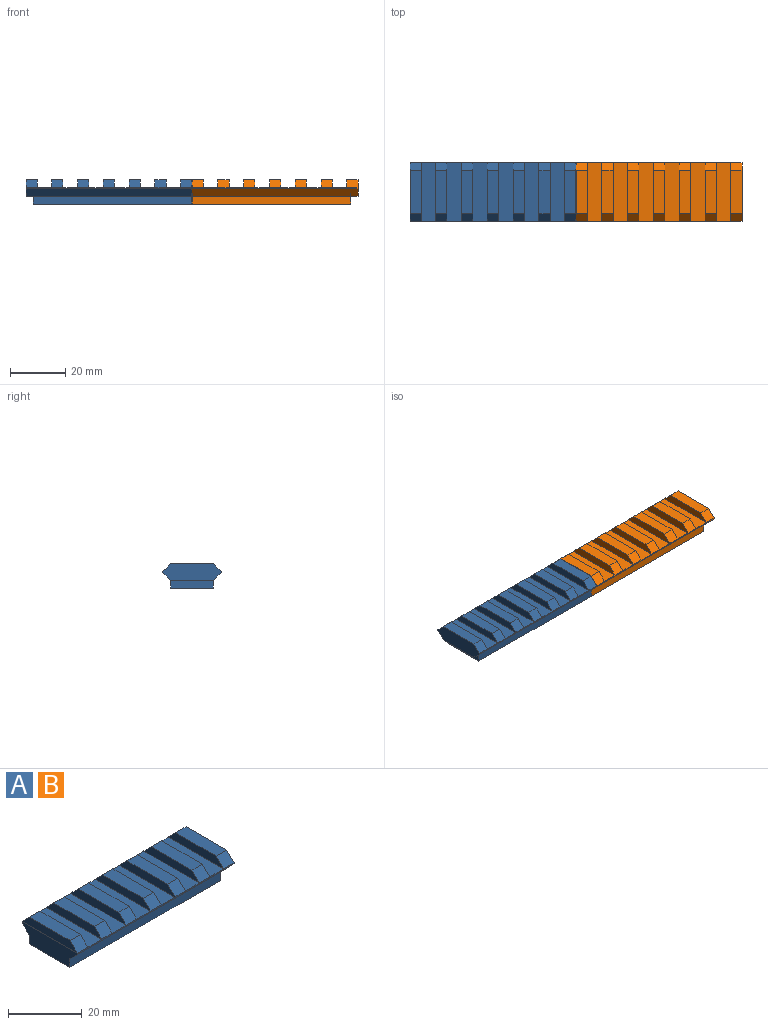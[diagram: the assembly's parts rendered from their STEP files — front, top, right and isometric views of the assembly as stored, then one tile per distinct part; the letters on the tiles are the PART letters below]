
ASSEMBLY  parts=2 mates=1
PART A: 54 faces, bbox 60.2x21.2x8.9 mm
  f0: plane 21.2x5.99mm, normal (-1,0,0), area 103mm2, adj f1,f3,f5,f6,f34,f44,f51,f52
  f1: plane 57.6x15.57mm, normal (0,0,-1), area 897.1mm2, adj f0,f2,f51,f53
  f2: plane 18.39x5.66mm, normal (1,0,0), area 44.7mm2, adj f1,f3,f5,f35,f37,f44,f51,f52
  f3: plane 57.6x2.79mm, normal (0,-0.71,-0.71), area 227.7mm2, adj f0,f2,f5,f52
  f4: plane 15.6x4.01mm, normal (0,0,1), area 62.4mm2, adj f11,f12,f13,f50
  f5: plane 60.17x0.4mm, normal (0,-1,0), area 22.1mm2, adj f0,f2,f3,f11,f12,f14,f15,f16
  f6: plane 60.17x0.4mm, normal (0,1,0), area 21.1mm2, adj f0,f11,f12,f13,f14,f15,f16,f17
  f7: plane 15.6x4.01mm, normal (0,0,1), area 62.4mm2, adj f15,f16,f17,f49
  f8: plane 15.6x4.01mm, normal (0,0,1), area 62.4mm2, adj f19,f20,f21,f48
  f9: plane 15.6x4.01mm, normal (0,0,1), area 62.4mm2, adj f36,f38,f39,f45
  f10: plane 15.6x4.01mm, normal (0,0,1), area 62.4mm2, adj f40,f41,f42,f43
  f11: plane 21.2x2.88mm, normal (-1,0,0), area 53.2mm2, adj f4,f5,f6,f13,f14,f50
  f12: plane 21.2x2.89mm, normal (1,0,0), area 53.1mm2, adj f4,f5,f6,f13,f18,f50
  f13: plane 4x2.8mm, normal (0,0.71,0.71), area 15.8mm2, adj f4,f6,f11,f12
  f14: plane 21.2x5.35mm, normal (0,0,1), area 113.4mm2, adj f5,f6,f11,f24
  f15: plane 21.2x2.88mm, normal (-1,0,0), area 53.2mm2, adj f5,f6,f7,f17,f18,f49
  f16: plane 21.2x2.89mm, normal (1,0,0), area 53.1mm2, adj f5,f6,f7,f17,f22,f49
  f17: plane 4x2.8mm, normal (0,0.71,0.71), area 15.8mm2, adj f6,f7,f15,f16
  f18: plane 21.2x5.35mm, normal (0,0,1), area 113.4mm2, adj f5,f6,f12,f15
  f19: plane 21.2x2.88mm, normal (-1,0,0), area 53.2mm2, adj f5,f6,f8,f21,f22,f48
  f20: plane 21.2x2.89mm, normal (1,0,0), area 53.1mm2, adj f5,f6,f8,f21,f23,f48
  f21: plane 4x2.8mm, normal (0,0.71,0.71), area 15.8mm2, adj f6,f8,f19,f20
  f22: plane 21.2x5.35mm, normal (0,0,1), area 113.4mm2, adj f5,f6,f16,f19
  f23: plane 21.2x5.35mm, normal (0,0,1), area 113.4mm2, adj f5,f6,f20,f40
  f24: plane 21.2x2.88mm, normal (1,0,0), area 53.2mm2, adj f5,f6,f14,f26,f27,f47
  f25: plane 21.2x2.88mm, normal (-1,0,0), area 53.1mm2, adj f5,f6,f26,f27,f29,f47
  f26: plane 15.6x4.01mm, normal (0,0,1), area 62.4mm2, adj f24,f25,f27,f47
  f27: plane 4x2.79mm, normal (0,0.71,0.71), area 15.8mm2, adj f6,f24,f25,f26
  f28: plane 21.2x5.35mm, normal (0,0,1), area 113.4mm2, adj f5,f6,f36,f41
  f29: plane 21.2x5.35mm, normal (0,0,1), area 113.4mm2, adj f5,f6,f25,f31
  f30: plane 21.2x2.88mm, normal (-1,0,0), area 53.1mm2, adj f5,f6,f32,f33,f34,f46
  f31: plane 21.2x2.88mm, normal (1,0,0), area 53.2mm2, adj f5,f6,f29,f32,f33,f46
  f32: plane 15.6x4.01mm, normal (0,0,1), area 62.4mm2, adj f30,f31,f33,f46
  f33: plane 4x2.79mm, normal (0,0.71,0.71), area 15.8mm2, adj f6,f30,f31,f32
  f34: plane 21.2x0.07mm, normal (0,0,1), area 1.4mm2, adj f0,f5,f6,f30
  f35: plane 15.59x2.57mm, normal (0,0,-1), area 40mm2, adj f2,f37,f38,f44
  f36: plane 21.2x2.88mm, normal (-1,0,0), area 53.1mm2, adj f5,f6,f9,f28,f39,f45
  f37: plane 2.8x2.8mm, normal (0,-0.71,-0.71), area 10.1mm2, adj f2,f5,f35,f38
  f38: plane 21.2x6.01mm, normal (1,0,0), area 111.5mm2, adj f5,f6,f9,f35,f37,f39,f44,f45
  f39: plane 4x2.8mm, normal (0,0.71,0.71), area 15.8mm2, adj f6,f9,f36,f38
  f40: plane 21.2x2.88mm, normal (-1,0,0), area 53.2mm2, adj f5,f6,f10,f23,f42,f43
  f41: plane 21.2x2.89mm, normal (1,0,0), area 53.1mm2, adj f5,f6,f10,f28,f42,f43
  f42: plane 4x2.8mm, normal (0,0.71,0.71), area 15.8mm2, adj f6,f10,f40,f41
  f43: plane 4.01x2.83mm, normal (0,-0.71,0.71), area 16mm2, adj f5,f10,f40,f41
  f44: plane 60.17x2.83mm, normal (0,0.71,-0.71), area 240.4mm2, adj f0,f2,f6,f35,f38,f53
  f45: plane 4.01x2.83mm, normal (0,-0.71,0.71), area 16mm2, adj f5,f9,f36,f38
  f46: plane 4.01x2.83mm, normal (0,-0.71,0.71), area 16mm2, adj f5,f30,f31,f32
  f47: plane 4.01x2.83mm, normal (0,-0.71,0.71), area 16mm2, adj f5,f24,f25,f26
  f48: plane 4.01x2.83mm, normal (0,-0.71,0.71), area 16mm2, adj f5,f8,f19,f20
  f49: plane 4.01x2.83mm, normal (0,-0.71,0.71), area 16mm2, adj f5,f7,f15,f16
  f50: plane 4.01x2.83mm, normal (0,-0.71,0.71), area 16mm2, adj f4,f5,f11,f12
  f51: plane 57.6x2.85mm, normal (0,-1,0), area 164.1mm2, adj f0,f1,f2,f52
  f52: plane 57.6x0.01mm, normal (0,-0.06,-1), area 0.3mm2, adj f0,f2,f3,f51
  f53: plane 57.6x2.85mm, normal (0,1,0), area 164.1mm2, adj f0,f1,f2,f44
PART B: same geometry as A
PLACE A rot(axis=(0,0,-1),180deg) t=(-80.68,-21.9,13.97)mm
PLACE B t=(-25.08,-21.87,13.97)mm
MATE fastened A.f0 <-> B.f0  axis (1,0,0) through (-52.88,-21.88,18.47)mm
